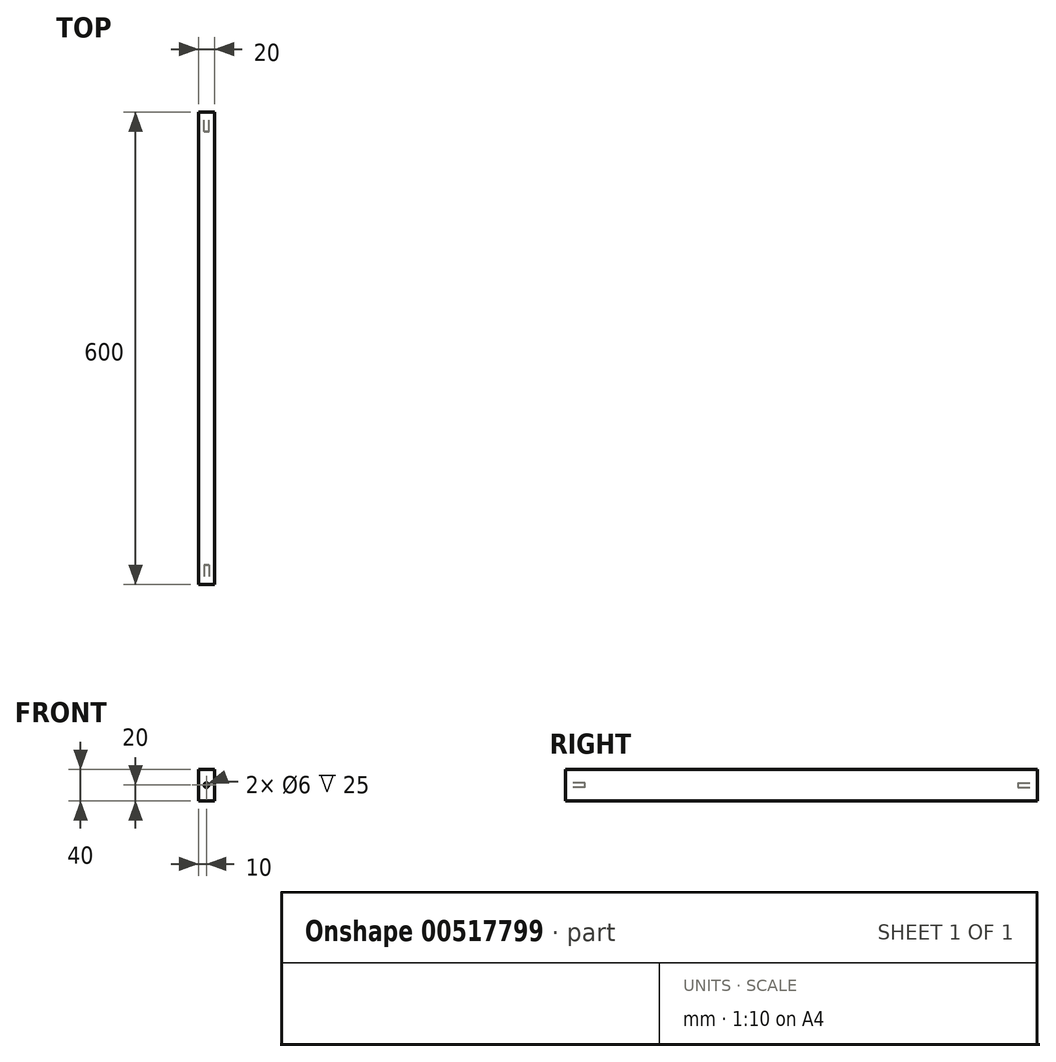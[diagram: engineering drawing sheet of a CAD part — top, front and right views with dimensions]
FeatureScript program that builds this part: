
annotation { "Feature Type Name" : "Feature", "Feature Type Description" : "" }
export const myFeature = defineFeature(function(context is Context, id is Id, definition is map)
    precondition{}
    {
        {
            var Q0;
            Q0=qCreatedBy(makeId("Front.planeOp"),FACE);
            var sketch = newSketch(context, id + "F0", { "sketchPlane" : qUnion([Q0])});
            skLineSegment(sketch, "E0.bottom", {"start": v(0, 0) * mm, "end": v(-20, 0) * mm});
            skLineSegment(sketch, "E0.top", {"start": v(0, 40) * mm, "end": v(-20, 40) * mm});
            skLineSegment(sketch, "E0.left", {"start": v(0, 0) * mm, "end": v(0, 40) * mm});
            skLineSegment(sketch, "E0.right", {"start": v(-20, 0) * mm, "end": v(-20, 40) * mm});
            skSolve(sketch);
        }
        {
            var Q0;
            Q0 = qSketchRegion(id + "F0", true);
            extrude(context, id + "F1", {"entities" : qUnion([Q0]), "depth" : 600 * mm, "offsetDistance" : 25 * mm});
        }
        {
            var Q0;
            Q0=makeQuery(id+"F1.opExtrude","CAP_FACE",FACE,{"disambiguationData":[OSD([sQuery(id+"F0.wireOp",EDGE,"E0.bottom"),sQuery(id+"F0.wireOp",EDGE,"E0.top"),sQuery(id+"F0.wireOp",EDGE,"E0.left"),sQuery(id+"F0.wireOp",EDGE,"E0.right")])],"isStart":true});
            var sketch = newSketch(context, id + "F2", { "sketchPlane" : qUnion([Q0])});
            skCircle(sketch, "E1", {"center": v(10, 20) * mm, "radius": 3 * mm});
            skPoint(sketch, "E1.centerSnap0", {"position": v(10, 40) * mm});
            skPoint(sketch, "E1.centerSnap1", {"position": v(0, 20) * mm});
            skSolve(sketch);
        }
        {
            var Q0;
            Q0=makeQuery(id+"F2.imprint","IMPRINT",FACE,{"disambiguationData":[TD([[makeQuery(id+"F2.imprint","IMPRINT",EDGE,{"derivedFrom":sQuery(id+"F2.wireOp",EDGE,"E1")}),1.0]])]});
            extrude(context, id + "F3", {"entities" : qUnion([Q0]), "operationType" : NewBodyOperationType.REMOVE, "oppositeDirection" : true, "depth" : 25 * mm, "offsetDistance" : 25 * mm});
        }
        {
            var Q0;
            Q0=makeQuery(id+"F1.opExtrude","CAP_FACE",FACE,{"disambiguationData":[OSD([sQuery(id+"F0.wireOp",EDGE,"E0.bottom"),sQuery(id+"F0.wireOp",EDGE,"E0.top"),sQuery(id+"F0.wireOp",EDGE,"E0.left"),sQuery(id+"F0.wireOp",EDGE,"E0.right")])],"isStart":false});
            var sketch = newSketch(context, id + "F4", { "sketchPlane" : qUnion([Q0])});
            skCircle(sketch, "E2", {"center": v(-10, 20) * mm, "radius": 3 * mm});
            skPoint(sketch, "E2.centerSnap0", {"position": v(-20, 20) * mm});
            skPoint(sketch, "E2.centerSnap1", {"position": v(-10, 40) * mm});
            skSolve(sketch);
        }
        {
            var Q0;
            Q0=makeQuery(id+"F4.imprint","IMPRINT",FACE,{"disambiguationData":[TD([[makeQuery(id+"F4.imprint","IMPRINT",EDGE,{"derivedFrom":sQuery(id+"F4.wireOp",EDGE,"E2")}),1.0]])]});
            extrude(context, id + "F5", {"entities" : qUnion([Q0]), "operationType" : NewBodyOperationType.REMOVE, "oppositeDirection" : true, "depth" : 25 * mm, "offsetDistance" : 25 * mm});
        }
    });
